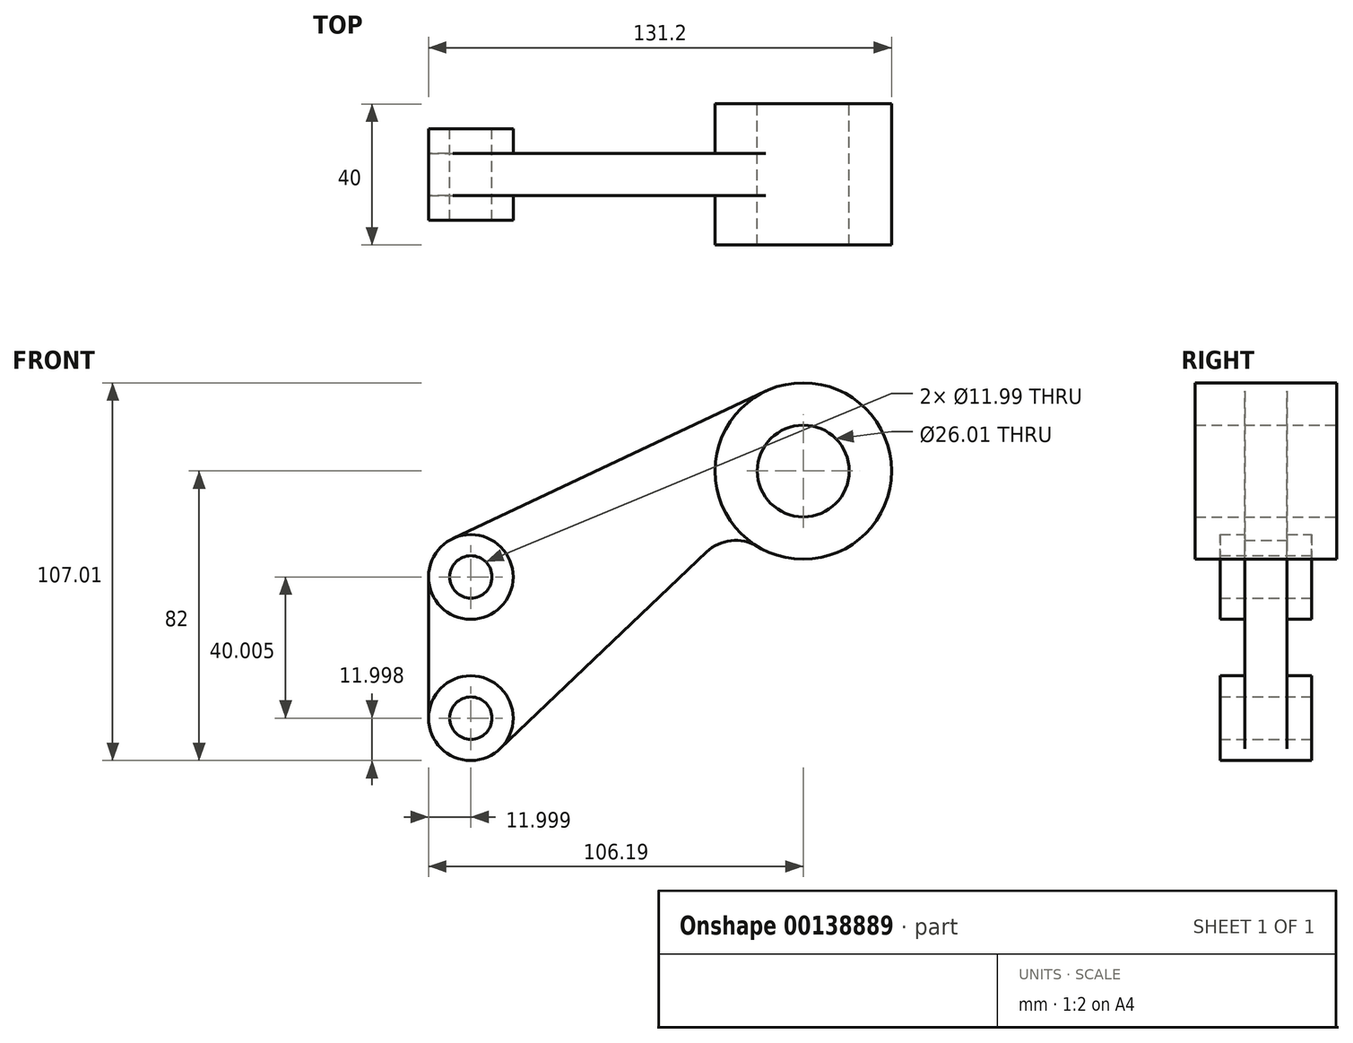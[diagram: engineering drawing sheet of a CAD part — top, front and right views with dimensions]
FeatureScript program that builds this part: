
annotation { "Feature Type Name" : "Feature", "Feature Type Description" : "" }
export const myFeature = defineFeature(function(context is Context, id is Id, definition is map)
    precondition{}
    {
        {
            var Q0;
            Q0=qCreatedBy(makeId("Front.planeOp"),FACE);
            var sketch = newSketch(context, id + "F0", { "sketchPlane" : qUnion([Q0])});
            skCircle(sketch, "E0", {"center": v(0, 0) * mm, "radius": 13 * mm});
            skCircle(sketch, "E1", {"center": v(0, 0) * mm, "radius": 25 * mm});
            skCircle(sketch, "E2", {"center": v(-94.2, -30) * mm, "radius": 6 * mm});
            skCircle(sketch, "E3", {"center": v(-94.2, -30) * mm, "radius": 12 * mm});
            skLineSegment(sketch, "E4", {"start": v(-99.3, -19.14) * mm, "end": v(-10.66, 22.62) * mm});
            skCircle(sketch, "E5", {"center": v(-94.2, -70) * mm, "radius": 6 * mm});
            skCircle(sketch, "E6", {"center": v(-94.2, -70) * mm, "radius": 12 * mm});
            skLineSegment(sketch, "E7", {"start": v(-106.2, -30) * mm, "end": v(-106.2, -70) * mm});
            skLineSegment(sketch, "E8", {"start": v(-85.91, -78.7) * mm, "end": v(-27.43, -22.97) * mm});
            skArc(sketch, "E9", {"start": v(-27.43, -22.97) * mm, "mid": v(-20.46, -19.73) * mm, "end": v(-12.95, -21.4) * mm});
            skSolve(sketch);
        }
        {
            var Q0;
            Q0=makeQuery(id+"F0.imprint","IMPRINT",FACE,{"disambiguationData":[TD([[makeQuery(id+"F0.imprint","IMPRINT",EDGE,{"derivedFrom":sQuery(id+"F0.wireOp",EDGE,"E0")}),-1.0]])]});
            extrude(context, id + "F1", {"entities" : qUnion([Q0]), "endBound" : BoundingType.SYMMETRIC, "depth" : 40 * mm});
        }
        {
            var Q0;
            {var subQ3=sQuery(id+"F0.wireOp",EDGE,"E4");Q0=makeQuery(id+"F0.imprint","IMPRINT",FACE,{"disambiguationData":[TD([[makeQuery(id+"F0.imprint","IMPRINT",EDGE,{"derivedFrom":subQ3}),-1.0]])]});}
            extrude(context, id + "F2", {"entities" : qUnion([Q0]), "operationType" : NewBodyOperationType.ADD, "endBound" : BoundingType.SYMMETRIC, "depth" : 12 * mm});
        }
        {
            var Q0;
            Q0=makeQuery(id+"F0.imprint","IMPRINT",FACE,{"disambiguationData":[TD([[makeQuery(id+"F0.imprint","IMPRINT",EDGE,{"derivedFrom":sQuery(id+"F0.wireOp",EDGE,"E2")}),-1.0]])]});
            var Q1;
            Q1=makeQuery(id+"F0.imprint","IMPRINT",FACE,{"disambiguationData":[TD([[makeQuery(id+"F0.imprint","IMPRINT",EDGE,{"derivedFrom":sQuery(id+"F0.wireOp",EDGE,"E5")}),-1.0]])]});
            extrude(context, id + "F3", {"entities" : qUnion([Q0, Q1]), "operationType" : NewBodyOperationType.ADD, "endBound" : BoundingType.SYMMETRIC, "depth" : 26 * mm});
        }
    });
